# Revit family: 210_aa2a3770aa9444c5a1c09640491d79
name_source: partatom
category: Mechanical Equipment
revit_build: Autodesk Revit 2018 (Build: 20170223_1515(x64)
units: mm (PartAtom-declared; Revit-internal decimal feet)

## family parameters
Always vertical = Yes
Classification = None
Cut with Voids When Loaded = No
Part Type = Breaks Into
Room Calculation Point = No
Round Connector Dimension = Use Diameter
Shared = No
Work Plane-Based = No

## types (1)
- 04040
    DI = 51 mm
    DO = 51 mm
    DZ1 = 400 mm  [stored 1.31234 ft]
    DZ2 = 326 mm  [stored 1.06955 ft]
    Description = Central Vacuum Cleaner CVR 4000
    H = 799 mm  [stored 2.62139 ft]
    L2 = 198 mm
    LB = 138 mm
    LB3 = 190 mm
    LT2 = 49 mm
    MC Product Code = 04040
    Manufacturer = Flexit
    QmdConnectorList = 201;DI;202;DO
    RI = 26 mm
    RO = 26 mm
    URL = www.flexit.no
    W = 461 mm  [stored 1.51247 ft]
    W1 = 66 mm  [stored 0.216535 ft]
    W11 = 116 mm  [stored 0.380577 ft]
    W22 = 235 mm
    magiPartTypeId = 210
    magiProductFamilyId = aa2a3770aa9444c5a1c09640491d79
    magiProductId = 2422022f4d474525af27f15fee3787

note: [stored X ft] marks values corroborated as IEEE doubles in the binary element streams (Revit-internal decimal feet)

## geometry (parser evidence)
native form markers: Sweep x2
no freeform markers — native parametric forms only
